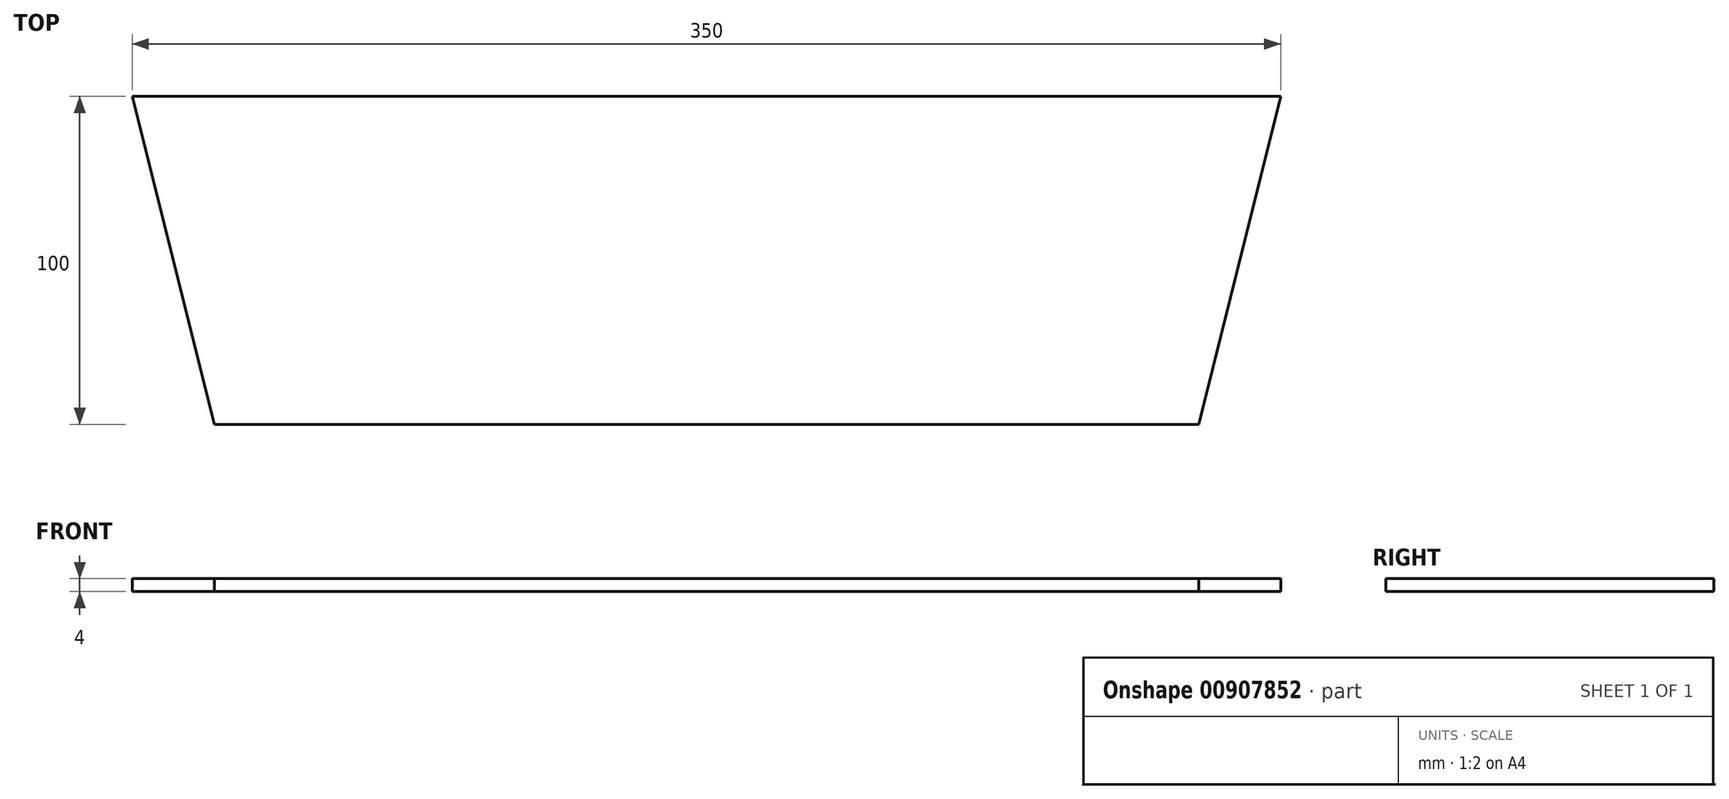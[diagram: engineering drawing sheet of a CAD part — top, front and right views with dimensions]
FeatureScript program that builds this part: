
annotation { "Feature Type Name" : "Feature", "Feature Type Description" : "" }
export const myFeature = defineFeature(function(context is Context, id is Id, definition is map)
    precondition{}
    {
        {
            var Q0;
            Q0=qCreatedBy(makeId("Top.planeOp"),FACE);
            var sketch = newSketch(context, id + "F0", { "sketchPlane" : qUnion([Q0])});
            skLineSegment(sketch, "E0", {"start": v(0, 0) * mm, "end": v(150, 0) * mm});
            skLineSegment(sketch, "E1", {"start": v(0, 0) * mm, "end": v(-150, 0) * mm});
            skLineSegment(sketch, "E2", {"start": v(0, 100) * mm, "end": v(175, 100) * mm});
            skLineSegment(sketch, "E3", {"start": v(175, 100) * mm, "end": v(150, 0) * mm});
            skLineSegment(sketch, "E4", {"start": v(0, 100) * mm, "end": v(-175, 100) * mm});
            skLineSegment(sketch, "E5", {"start": v(-175, 100) * mm, "end": v(-150, 0) * mm});
            skSolve(sketch);
        }
        {
            var Q0;
            Q0=makeQuery(id+"F0.imprint","IMPRINT",FACE,{"disambiguationData":[TD([[makeQuery(id+"F0.imprint","IMPRINT",EDGE,{"derivedFrom":sQuery(id+"F0.wireOp",EDGE,"E0")}),1.0]])]});
            extrude(context, id + "F1", {"entities" : qUnion([Q0]), "depth" : 4 * mm, "offsetDistance" : 25 * mm});
        }
    });
